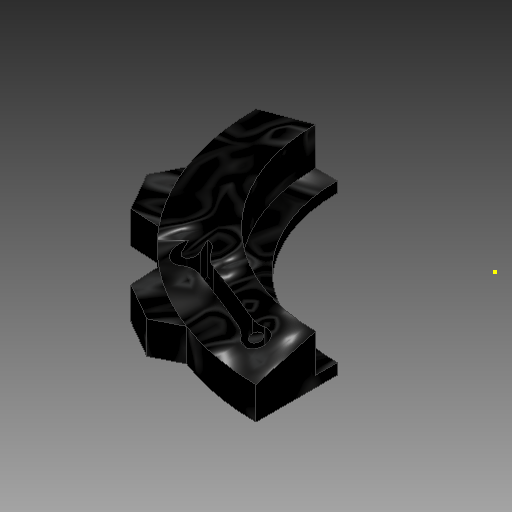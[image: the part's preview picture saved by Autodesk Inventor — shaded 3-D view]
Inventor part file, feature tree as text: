
AUTODESK INVENTOR PART (.ipt)
format: ipt  version: 2017 (Build 210142000, 142)  size: 348,672 bytes
history: native  units: in
note: dims shown in document units (in); Inventor stores cm internally (conversion verified against a paired STEP export)
features: sketch x6, extrude x4, projected_geometry x3, pattern_circular x2, revolve x1, plane x1, fillet x1, mirror x1
ambient origin geometry x8: Origin, YZ Plane, XZ Plane, XY Plane, X Axis, Y Axis, Z Axis, Center Point
bodies: Solid1 (feature_tree)
feature tree (19):
  revolve  "Revolution1"  [1 undecoded]
  plane  "Work Plane1"
  extrude  "Extrusion1"  Depth=0.05in
  pattern_circular  "Circular Pattern1"  [2 undecoded]
  extrude  "Extrusion3"  Depth=0.125in
  fillet  "Fillet1"  Radius=0.1in
  pattern_circular  "Circular Pattern2"  [2 undecoded]
  mirror  "Mirror1"
  extrude  "Extrusion4"  Depth=0.125in TaperAngle=360.0deg
  extrude  "Extrusion5"  Depth=0.125in
  sketch  "Sketch7"  dims[d7=0.1in d8=0.35in d9=0.2in d10=0.1in d11=1.0in d12=0.0in d13=4.7244in d14=360.0deg d19=0.1in d20=0.025in d22=0.15in d23=0.25in d24=0.14in d25=135.0deg d26=0.05in d27=0.025in d28=0.5in d29=0.2in d30=0.065in d31=1.0in d32=0.0in d33=0.125in d34=1.1811in d35=90.0deg d37=0.0in d38=0.0in d39=0.0in d40=0.0in]
  sketch  "Sketch1"  dims[d0=0.8265in d1=0.175in]
  sketch  "Sketch2"  dims[d2=0.05in d3=0.1in]
  sketch  "Sketch4"  dims[d4=0.15in]
  projected_geometry  "Projected Loop3"
  projected_geometry  "Projected Loop4"
  sketch  "Sketch5"  dims[d5=0.275in]
  sketch  "Sketch6"  dims[d6=90.0deg]
  projected_geometry  "Projected Loop5"
note: 5 required parameter values undecoded (feature->parameter linkage not recoverable at this tier; creation-order binding heuristic only, values carry confidence <= 0.55)